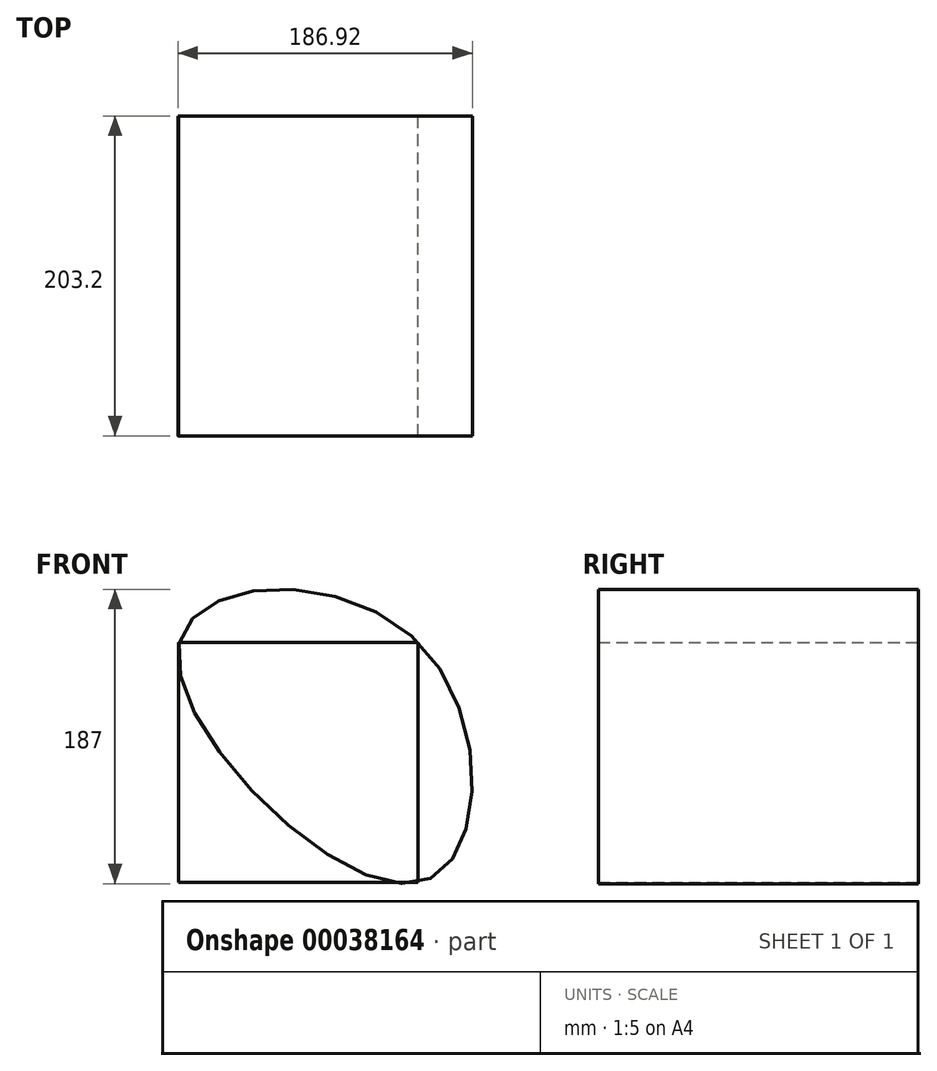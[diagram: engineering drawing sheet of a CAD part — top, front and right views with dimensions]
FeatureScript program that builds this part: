
annotation { "Feature Type Name" : "Feature", "Feature Type Description" : "" }
export const myFeature = defineFeature(function(context is Context, id is Id, definition is map)
    precondition{}
    {
        {
            var Q0;
            Q0=qCreatedBy(makeId("Front.planeOp"),FACE);
            var sketch = newSketch(context, id + "F0", { "sketchPlane" : qUnion([Q0])});
            skLineSegment(sketch, "E0.bottom", {"start": v(-75.86, 76.32) * mm, "end": v(76.17, 76.32) * mm});
            skLineSegment(sketch, "E0.top", {"start": v(-75.86, -76.02) * mm, "end": v(76.17, -76.02) * mm});
            skLineSegment(sketch, "E0.left", {"start": v(-75.86, 76.32) * mm, "end": v(-75.86, -76.02) * mm});
            skLineSegment(sketch, "E0.right", {"start": v(76.17, 76.32) * mm, "end": v(76.17, -76.02) * mm});
            skSolve(sketch);
        }
        {
            var Q0;
            Q0=makeQuery(id+"F0.imprint","IMPRINT",FACE,{"disambiguationData":[TD([[makeQuery(id+"F0.imprint","IMPRINT",EDGE,{"derivedFrom":sQuery(id+"F0.wireOp",EDGE,"E0.bottom")}),-1.0]])]});
            var sketch = newSketch(context, id + "F1", { "sketchPlane" : qUnion([Q0])});
            skFitSpline(sketch, "E1", {"points": [v(-75.56, 75.71) * mm, v(76.79, -76.02) * mm, v(76.17, 76.63) * mm, v(-75.56, 75.71) * mm]});
            skSolve(sketch);
        }
        {
            var Q0;
            Q0 = qSketchRegion(id + "F0", true);
            var Q1;
            Q1 = qSketchRegion(id + "F1", true);
            extrude(context, id + "F2", {"entities" : qUnion([Q0, Q1]), "depth" : 203.2 * mm});
        }
    });
